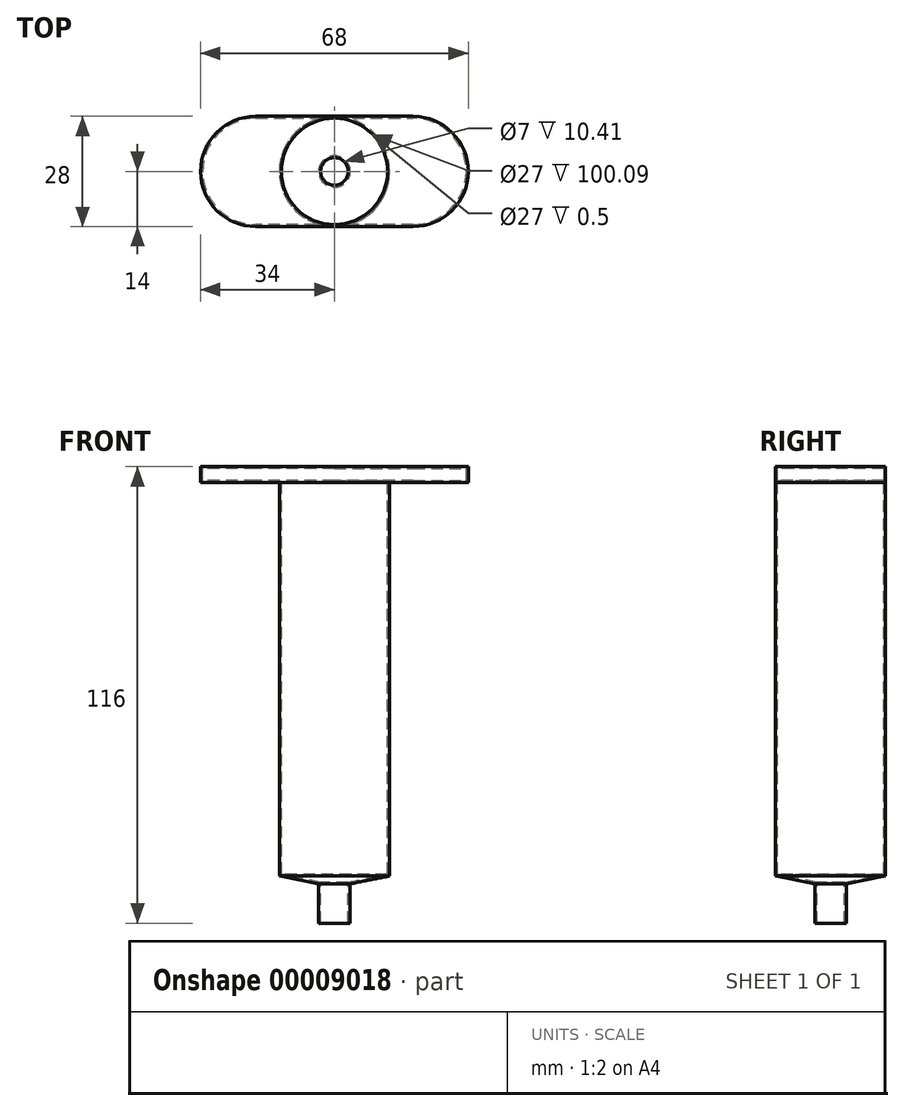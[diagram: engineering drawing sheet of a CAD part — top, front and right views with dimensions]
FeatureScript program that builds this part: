
annotation { "Feature Type Name" : "Feature", "Feature Type Description" : "" }
export const myFeature = defineFeature(function(context is Context, id is Id, definition is map)
    precondition{}
    {
        {
            var Q0;
            Q0=qCreatedBy(makeId("Front.planeOp"),FACE);
            var sketch = newSketch(context, id + "F0", { "sketchPlane" : qUnion([Q0])});
            skLineSegment(sketch, "E0", {"start": v(0, 0) * mm, "end": v(4, 0) * mm});
            skLineSegment(sketch, "E1", {"start": v(4, 0) * mm, "end": v(4, 10) * mm});
            skLineSegment(sketch, "E2", {"start": v(4, 10) * mm, "end": v(14, 12) * mm});
            skLineSegment(sketch, "E3", {"start": v(14, 12) * mm, "end": v(14, 112) * mm});
            skLineSegment(sketch, "E4", {"start": v(14, 112) * mm, "end": v(34, 112) * mm});
            skLineSegment(sketch, "E5", {"start": v(34, 112) * mm, "end": v(34, 116) * mm});
            skLineSegment(sketch, "E6", {"start": v(34, 116) * mm, "end": v(0, 116) * mm});
            skLineSegment(sketch, "E7", {"start": v(0, 116) * mm, "end": v(0, 0) * mm});
            skSolve(sketch);
        }
        {
            var Q0;
            Q0 = qSketchRegion(id + "F0", true);
            var Q1;
            Q1=sQuery(id+"F0.wireOp",EDGE,"E7");
            revolve(context, id + "F1", {"entities" : qUnion([Q0]), "axis" : qUnion([Q1]), "revolveType" : RevolveType.FULL});
        }
        {
            var Q0;
            Q0=makeQuery(id+"F1.opRevolve","SWEPT_FACE",FACE,{"disambiguationData":[OSD([sQuery(id+"F0.wireOp",EDGE,"E6")])]});
            var sketch = newSketch(context, id + "F2", { "sketchPlane" : qUnion([Q0])});
            skArc(sketch, "E8", {"start": v(-20, 14) * mm, "mid": v(-34, 0) * mm, "end": v(-20, -14) * mm});
            skArc(sketch, "E9", {"start": v(20, -14) * mm, "mid": v(34, 0) * mm, "end": v(20, 14) * mm});
            skLineSegment(sketch, "E10", {"start": v(-20, 14) * mm, "end": v(20, 14) * mm});
            skLineSegment(sketch, "E11", {"start": v(20, -14) * mm, "end": v(-20, -14) * mm});
            skSolve(sketch);
        }
        {
            var Q0;
            {var subQ5=sQuery(id+"F2.wireOp",EDGE,"E10");Q0=makeQuery(id+"F2.imprint","IMPRINT",FACE,{"disambiguationData":[TD([[makeQuery(id+"F2.imprint","IMPRINT",EDGE,{"derivedFrom":subQ5}),1.0]])]});}
            var Q1;
            {var subQ5=sQuery(id+"F2.wireOp",EDGE,"E11");Q1=makeQuery(id+"F2.imprint","IMPRINT",FACE,{"disambiguationData":[TD([[makeQuery(id+"F2.imprint","IMPRINT",EDGE,{"derivedFrom":subQ5}),1.0]])]});}
            extrude(context, id + "F3", {"entities" : qUnion([Q0, Q1]), "operationType" : NewBodyOperationType.REMOVE, "oppositeDirection" : true, "depth" : 25 * mm});
        }
        {
            var Q0;
            Q0=makeQuery(id+"F1.opRevolve","SWEPT_FACE",FACE,{"disambiguationData":[OSD([sQuery(id+"F0.wireOp",EDGE,"E0")])]});
            shell(context, id + "F4", {"entities" : qUnion([Q0]), "thickness" : 0.5 * mm});
        }
        {
            var Q0;
            Q0=makeQuery(id+"F1.opRevolve","SWEPT_FACE",FACE,{"disambiguationData":[OSD([sQuery(id+"F0.wireOp",EDGE,"E6")])]});
            var sketch = newSketch(context, id + "F5", { "sketchPlane" : qUnion([Q0])});
            skCircle(sketch, "E12", {"center": v(0, 0) * mm, "radius": 13.5 * mm});
            skSolve(sketch);
        }
        {
            var Q0;
            Q0 = qSketchRegion(id + "F5", true);
            extrude(context, id + "F6", {"entities" : qUnion([Q0]), "operationType" : NewBodyOperationType.REMOVE, "oppositeDirection" : true, "depth" : 25 * mm});
        }
    });
